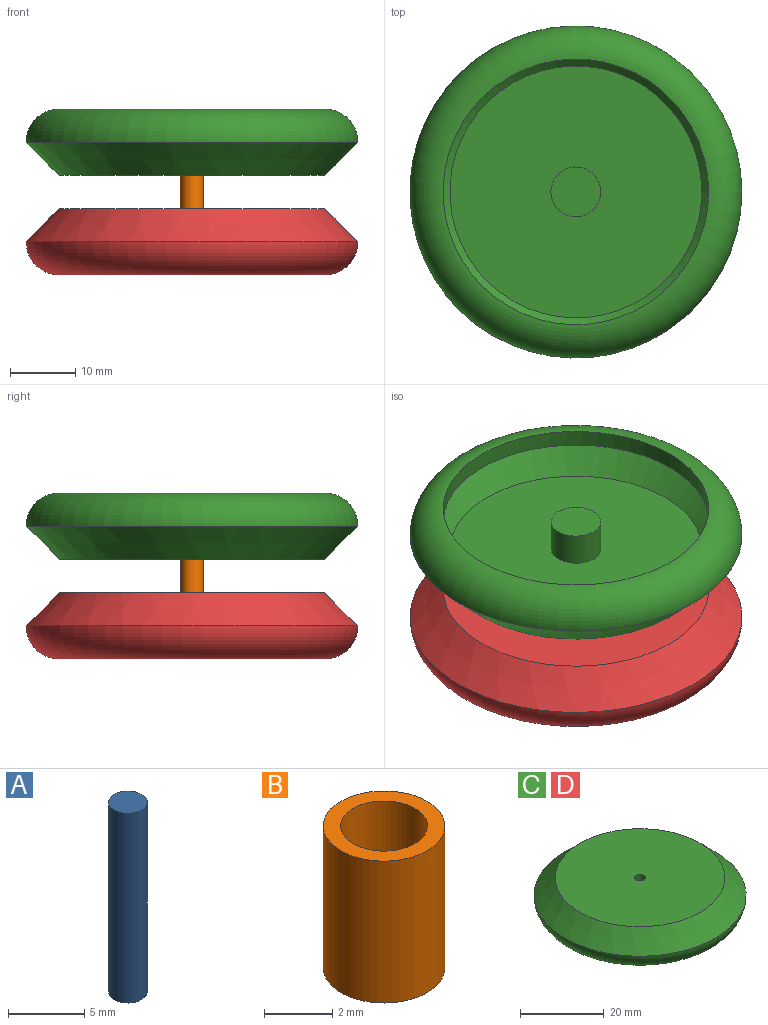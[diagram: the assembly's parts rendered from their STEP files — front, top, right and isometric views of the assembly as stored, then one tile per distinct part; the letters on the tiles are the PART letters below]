
ASSEMBLY  parts=4 mates=3
PART A: 3 faces, bbox 2.5x2.5x15.2 mm
  f0: cylinder r=1.27mm len=15.24mm, axis (0,0,-1), area 121.6mm2, adj f1,f2
  f1: plane 2.54x2.54mm, normal (0,0,1), area 5.1mm2, adj f0
  f2: plane 2.54x2.54mm, normal (0,0,-1), area 5.1mm2, adj f0
PART B: 4 faces, bbox 3.6x3.6x5.1 mm
  f0: cylinder r=1.27mm len=5.08mm, axis (0,0,-1), area 40.5mm2, adj f2,f3
  f1: cylinder r=1.78mm len=5.08mm, axis (0,0,-1), area 56.8mm2, adj f2,f3
  f2: plane 3.56x3.56mm, normal (0,0,1), area 4.9mm2, adj f0,f1
  f3: plane 3.56x3.56mm, normal (0,0,-1), area 4.9mm2, adj f0,f1
PART C: 11 faces, bbox 55x55x10.2 mm
  f0: plane 40.64x40.64mm, normal (0,0,1), area 1292.1mm2, adj f1,f3
  f1: cylinder r=1.27mm len=5.08mm, axis (0,0,1), area 40.5mm2, adj f0,f2
  f2: plane 2.54x2.54mm, normal (0,0,1), area 5.1mm2, adj f1
  f3: cone r=20.32mm half-angle=45deg, axis (0,0,-1), area 1031.9mm2, adj f0,f4
  f4: torus R=20.32mm, axis (0,0,1), area 1180.9mm2, adj f3,f5
  f5: cylinder r=20.32mm len=40.64mm, axis (0,0,1), area 324.3mm2, adj f4,f10
  f6: plane 38.54x38.54mm, normal (0,0,-1), area 1120.7mm2, adj f7,f9
  f7: cylinder r=3.81mm len=7.62mm, axis (0,0,1), area 121.6mm2, adj f6,f8
  f8: plane 7.62x7.62mm, normal (0,0,-1), area 45.6mm2, adj f7
  f9: cone r=18.52mm half-angle=45deg, axis (0,0,-1), area 639.7mm2, adj f6,f10
  f10: torus R=20.32mm, axis (0,0,1), area 419.5mm2, adj f5,f9
PART D: same geometry as C
PLACE A t=(11.8,-3,19.26)mm
PLACE B t=(11.8,-3,24.34)mm
PLACE C rot(axis=(1,0,0),180deg) t=(11.8,-3,39.58)mm
PLACE D t=(11.8,-3,14.18)mm
MATE fastened A.f0 <-> D.f1  axis (0,0,-1) through (11.8,-3,19.26)mm
MATE revolute B.f0 <-> A.f0  axis (0,0,-1) through (11.8,-3,26.88)mm
MATE fastened C.f1 <-> A.f0  axis (0,0,-1) through (11.8,-3,34.5)mm
